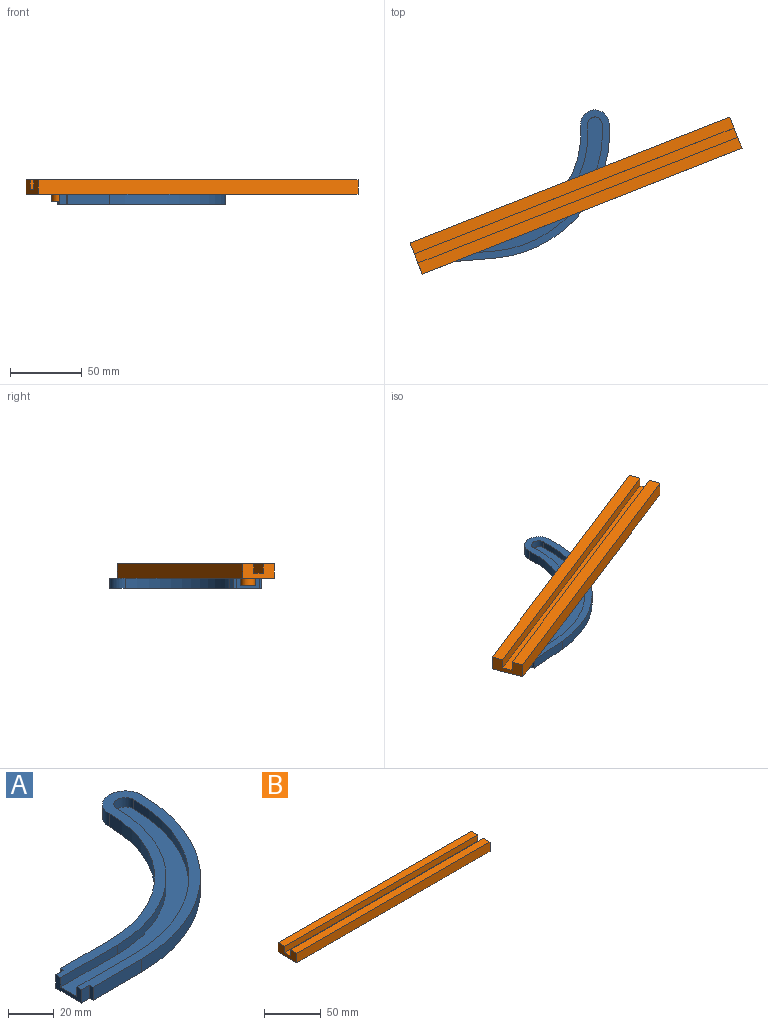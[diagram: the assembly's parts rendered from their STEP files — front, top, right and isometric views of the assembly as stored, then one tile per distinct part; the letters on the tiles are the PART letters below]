
ASSEMBLY  parts=2 mates=1
PART A: 18 faces, bbox 122.8x97.8x7 mm
  f0: plane 117.78x87.83mm, normal (0,0,1), area 1611.5mm2, adj f4,f5,f8,f9,f12,f15
  f1: plane 122.78x97.78mm, normal (0,0,-1), area 3280.7mm2, adj f2,f6,f7,f10,f11,f13,f14,f15
  f2: plane 30x7mm, normal (0,1,0), area 210mm2, adj f1,f3,f7,f17
  f3: plane 122.78x97.78mm, normal (0,0,1), area 1669.1mm2, adj f2,f4,f5,f6,f7,f8,f9,f10
  f4: plane 35x5mm, normal (0,-1,0), area 175mm2, adj f0,f3,f8,f15
  f5: plane 35x5mm, normal (0,1,0), area 175mm2, adj f0,f3,f9,f15
  f6: plane 30x7mm, normal (0,-1,0), area 210mm2, adj f1,f3,f10,f13
  f7: cylinder r=67.78mm len=67.78mm, axis (0,0,1), area 745.3mm2, adj f1,f2,f3,f11
  f8: cylinder r=72.78mm len=72.78mm, axis (0,0,1), area 571.6mm2, adj f0,f3,f4,f12
  f9: cylinder r=82.78mm len=82.78mm, axis (0,0,1), area 650.2mm2, adj f0,f3,f5,f12
  f10: cylinder r=87.78mm len=87.78mm, axis (0,0,1), area 965.2mm2, adj f1,f3,f6,f11
  f11: cylinder r=10mm len=20mm, axis (0,0,-1), area 219.9mm2, adj f1,f3,f7,f10
  f12: cylinder r=5mm len=10mm, axis (0,0,-1), area 79mm2, adj f0,f3,f8,f9
  f13: plane 7x2mm, normal (-1,0,0), area 14mm2, adj f1,f3,f6,f14
  f14: plane 7x5mm, normal (0,-1,0), area 35mm2, adj f1,f3,f13,f15
  f15: plane 16x7mm, normal (-1,0,0), area 62mm2, adj f0,f1,f3,f4,f5,f14,f16
  f16: plane 7x5mm, normal (0,1,0), area 35mm2, adj f1,f3,f15,f17
  f17: plane 7x2mm, normal (-1,0,0), area 14mm2, adj f1,f2,f3,f16
PART B: 14 faces, bbox 240x23.4x15.1 mm
  f0: plane 23.44x10.09mm, normal (-1,0,0), area 189.4mm2, adj f2,f3,f4,f5,f6,f7,f8,f9
  f1: plane 23.44x10.09mm, normal (1,0,0), area 189.4mm2, adj f2,f3,f4,f5,f6,f7,f8,f9
  f2: plane 240x23.44mm, normal (0,0,-1), area 5469.1mm2, adj f0,f1,f3,f9,f10,f12
  f3: plane 240x10.09mm, normal (0,1,0), area 2421.4mm2, adj f0,f1,f2,f4
  f4: plane 240x8.22mm, normal (0,0,1), area 1973.1mm2, adj f0,f1,f3,f5
  f5: plane 240x6.73mm, normal (0,-1,0), area 1614.2mm2, adj f0,f1,f4,f6
  f6: plane 240x7mm, normal (0,0,1), area 1680mm2, adj f0,f1,f5,f7
  f7: plane 240x6.73mm, normal (0,1,0), area 1614.2mm2, adj f0,f1,f6,f8
  f8: plane 240x8.22mm, normal (0,0,1), area 1973.1mm2, adj f0,f1,f7,f9
  f9: plane 240x10.09mm, normal (0,-1,0), area 2421.4mm2, adj f0,f1,f2,f8
  f10: cylinder r=5mm len=10mm, axis (0,0,1), area 157.1mm2, adj f2,f11
  f11: plane 10x10mm, normal (0,0,-1), area 78.5mm2, adj f10
  f12: cylinder r=5mm len=10mm, axis (0,0,1), area 157.1mm2, adj f2,f13
  f13: plane 10x10mm, normal (0,0,-1), area 78.5mm2, adj f12
PLACE A rot(axis=(0,0,1),4.6deg) t=(49.63,-215.45,-144.22)mm fixed
PLACE B rot(axis=(0,0,1),21.5deg) t=(107.8,-181.62,-137.22)mm
MATE parallel B.f2 <-> A.f3  axis (0,0,-1) through (109.13,-181.09,-137.22)mm
